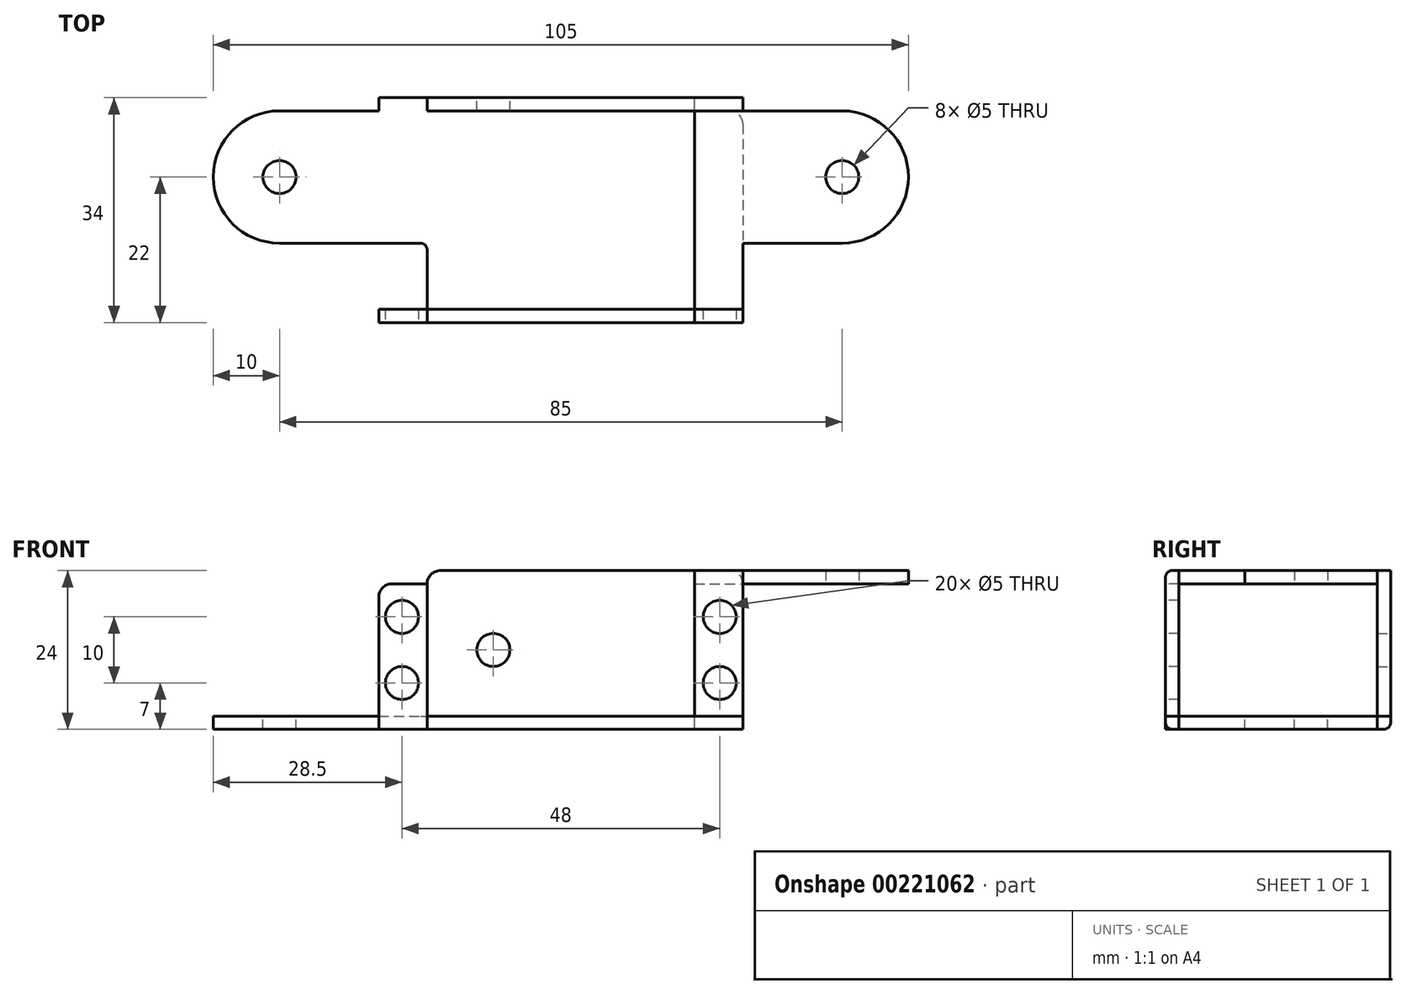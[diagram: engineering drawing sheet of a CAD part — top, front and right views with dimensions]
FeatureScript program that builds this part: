
annotation { "Feature Type Name" : "Feature", "Feature Type Description" : "" }
export const myFeature = defineFeature(function(context is Context, id is Id, definition is map)
    precondition{}
    {
        {
            var Q0;
            Q0=qCreatedBy(makeId("Front.planeOp"),FACE);
            var sketch = newSketch(context, id + "F0", { "sketchPlane" : qUnion([Q0])});
            skLineSegment(sketch, "E0.bottom", {"start": v(-27.5, 10) * mm, "end": v(-20.2, 10) * mm});
            skLineSegment(sketch, "E0.top", {"start": v(-27.5, -10) * mm, "end": v(27.5, -10) * mm});
            skLineSegment(sketch, "E0.left", {"start": v(-27.5, 10) * mm, "end": v(-27.5, -10) * mm});
            skLineSegment(sketch, "E0.right", {"start": v(27.5, 10) * mm, "end": v(27.5, -10) * mm});
            skLineSegment(sketch, "E1", {"start": v(-20.2, 10) * mm, "end": v(-20.2, -10) * mm});
            skLineSegment(sketch, "E2", {"start": v(20.2, 10) * mm, "end": v(20.2, -10) * mm});
            skCircle(sketch, "E3", {"center": v(-24, 5) * mm, "radius": 2.5 * mm});
            skCircle(sketch, "E4", {"center": v(-24, -5) * mm, "radius": 2.5 * mm});
            skCircle(sketch, "E5", {"center": v(24, 5) * mm, "radius": 2.5 * mm});
            skCircle(sketch, "E6", {"center": v(24, -5) * mm, "radius": 2.5 * mm});
            skLineSegment(sketch, "E7", {"start": v(-27.5, -10) * mm, "end": v(-27.5, -12) * mm});
            skLineSegment(sketch, "E8", {"start": v(-27.5, -12) * mm, "end": v(27.5, -12) * mm});
            skLineSegment(sketch, "E9", {"start": v(27.5, -12) * mm, "end": v(27.5, -10) * mm});
            skLineSegment(sketch, "E10", {"start": v(20.2, 10) * mm, "end": v(20.2, 12) * mm});
            skLineSegment(sketch, "E11", {"start": v(20.2, 12) * mm, "end": v(27.5, 12) * mm});
            skLineSegment(sketch, "E12", {"start": v(27.5, 12) * mm, "end": v(27.5, 10) * mm});
            skLineSegment(sketch, "E13.trimOffspring", {"start": v(20.2, 10) * mm, "end": v(27.5, 10) * mm});
            skSolve(sketch);
        }
        {
            var Q0;
            Q0=qCreatedBy(makeId("Top.planeOp"),FACE);
            var sketch = newSketch(context, id + "F1", { "sketchPlane" : qUnion([Q0])});
            skLineSegment(sketch, "E14", {"start": v(-27.5, 34) * mm, "end": v(-27.5, 2) * mm});
            skLineSegment(sketch, "E15", {"start": v(-27.5, 2) * mm, "end": v(20.2, 2) * mm});
            skLineSegment(sketch, "E16", {"start": v(-27.5, 32) * mm, "end": v(42.5, 32) * mm});
            skLineSegment(sketch, "E17", {"start": v(-27.5, 2) * mm, "end": v(-27.5, 0) * mm});
            skLineSegment(sketch, "E18", {"start": v(-27.5, 0) * mm, "end": v(27.5, 0) * mm});
            skCircle(sketch, "E19", {"center": v(42.5, 22) * mm, "radius": 2.5 * mm});
            skLineSegment(sketch, "E20", {"start": v(-27.5, 34) * mm, "end": v(27.5, 34) * mm});
            skLineSegment(sketch, "E21", {"start": v(27.5, 34) * mm, "end": v(27.5, 32) * mm});
            skLineSegment(sketch, "E22", {"start": v(42.5, 12) * mm, "end": v(42.5, 12) * mm});
            skLineSegment(sketch, "E23", {"start": v(42.5, 12) * mm, "end": v(20.2, 12) * mm});
            skLineSegment(sketch, "E24", {"start": v(20.2, 12) * mm, "end": v(20.2, 32) * mm});
            skLineSegment(sketch, "E25", {"start": v(20.2, 12) * mm, "end": v(20.2, 2) * mm});
            skLineSegment(sketch, "E26", {"start": v(20.2, 2) * mm, "end": v(20.2, 0) * mm});
            skLineSegment(sketch, "E27", {"start": v(-20.2, 2) * mm, "end": v(-20.2, 0) * mm});
            skLineSegment(sketch, "E28", {"start": v(-20.2, 32) * mm, "end": v(-20.2, 34) * mm});
            skArc(sketch, "E29", {"start": v(42.5, 12) * mm, "mid": v(52.5, 22) * mm, "end": v(42.5, 32) * mm});
            skLineSegment(sketch, "E30", {"start": v(20.2, 2) * mm, "end": v(27.5, 2) * mm});
            skLineSegment(sketch, "E31", {"start": v(27.5, 2) * mm, "end": v(27.5, 12) * mm});
            skLineSegment(sketch, "E32", {"start": v(27.5, 12) * mm, "end": v(27.5, 2) * mm});
            skLineSegment(sketch, "E33", {"start": v(27.5, 0) * mm, "end": v(27.5, 2) * mm});
            skSolve(sketch);
        }
        {
            var Q0;
            Q0=makeQuery(id+"F0.imprint","IMPRINT",FACE,{"disambiguationData":[TD([[makeQuery(id+"F0.imprint","IMPRINT",EDGE,{"derivedFrom":sQuery(id+"F0.wireOp",EDGE,"E0.bottom")}),-1.0]])]});
            var Q1;
            {var subQ0=sQuery(id+"F0.wireOp",EDGE,"E7");Q1=makeQuery(id+"F0.imprint","IMPRINT",FACE,{"disambiguationData":[TD([[makeQuery(id+"F0.imprint","IMPRINT",EDGE,{"derivedFrom":subQ0}),1.0]])]});}
            var Q2;
            {var subQ0=sQuery(id+"F0.wireOp",EDGE,"E0.right");Q2=makeQuery(id+"F0.imprint","IMPRINT",FACE,{"disambiguationData":[TD([[makeQuery(id+"F0.imprint","IMPRINT",EDGE,{"derivedFrom":subQ0}),-1.0]])]});}
            var Q3;
            Q3=makeQuery(id+"F0.imprint","IMPRINT",FACE,{"disambiguationData":[TD([[makeQuery(id+"F0.imprint","IMPRINT",EDGE,{"derivedFrom":sQuery(id+"F0.wireOp",EDGE,"E10")}),-1.0]])]});
            extrude(context, id + "F2", {"entities" : qUnion([Q0, Q1, Q2, Q3]), "oppositeDirection" : true, "depth" : 2 * mm});
        }
        {
            var Q0;
            {var subQ4=sQuery(id+"F1.wireOp",EDGE,"E15");Q0=makeQuery(id+"F1.imprint","IMPRINT",FACE,{"disambiguationData":[TD([[makeQuery(id+"F1.imprint","IMPRINT",EDGE,{"derivedFrom":subQ4}),1.0]])]});}
            var Q1;
            {var subQ8=sQuery(id+"F1.wireOp",EDGE,"E23");Q1=makeQuery(id+"F1.imprint","IMPRINT",FACE,{"disambiguationData":[TD([[makeQuery(id+"F1.imprint","IMPRINT",EDGE,{"derivedFrom":subQ8}),-1.0]])]});}
            var Q2;
            {var subQ0=sQuery(id+"F1.wireOp",EDGE,"E22");Q2=makeQuery(id+"F1.imprint","IMPRINT",FACE,{"disambiguationData":[TD([[makeQuery(id+"F1.imprint","IMPRINT",EDGE,{"derivedFrom":subQ0}),1.0]])]});}
            var Q3;
            {var subQ0=sQuery(id+"F1.wireOp",EDGE,"E21");Q3=makeQuery(id+"F1.imprint","IMPRINT",FACE,{"disambiguationData":[TD([[makeQuery(id+"F1.imprint","IMPRINT",EDGE,{"derivedFrom":subQ0}),-1.0]])]});}
            var Q4;
            {var subQ0=sQuery(id+"F1.wireOp",EDGE,"E26");Q4=makeQuery(id+"F1.imprint","IMPRINT",FACE,{"disambiguationData":[TD([[makeQuery(id+"F1.imprint","IMPRINT",EDGE,{"derivedFrom":subQ0}),-1.0]])]});}
            var Q5;
            {var subQ0=sQuery(id+"F1.wireOp",EDGE,"E17");Q5=makeQuery(id+"F1.imprint","IMPRINT",FACE,{"disambiguationData":[TD([[makeQuery(id+"F1.imprint","IMPRINT",EDGE,{"derivedFrom":subQ0}),1.0]])]});}
            extrude(context, id + "F3", {"entities" : qUnion([Q0, Q1, Q2, Q3, Q4, Q5]), "oppositeDirection" : true, "depth" : 2 * mm});
        }
        {
            var Q0;
            Q0=makeQuery(id+"F3.opExtrude","SWEPT_BODY",BODY,{"disambiguationData":[OSD([sQuery(id+"F1.wireOp",EDGE,"E14"),sQuery(id+"F1.wireOp",EDGE,"E15"),sQuery(id+"F1.wireOp",EDGE,"q6oPXj39-0zLh-izCR-QsKZ-P5NbTc8Rfou4"),sQuery(id+"F1.wireOp",EDGE,"E16"),sQuery(id+"F1.wireOp",EDGE,"E19"),sQuery(id+"F1.wireOp",EDGE,"E20"),sQuery(id+"F1.wireOp",EDGE,"E21"),sQuery(id+"F1.wireOp",EDGE,"E22")])]});
            var Q1;
            Q1=makeQuery(id+"F2.opExtrude","CAP_EDGE",EDGE,{"disambiguationData":[OSD([sQuery(id+"F0.wireOp",EDGE,"E0.left"),sQuery(id+"F0.wireOp",EDGE,"E7")])],"isStart":false});
            transform(context, id + "F4", {"entities" : qUnion([Q0]), "transformType" : TransformType.TRANSLATION_DISTANCE, "transformDirection" : qUnion([Q1]), "distance" : 10 * mm, "makeCopy" : false});
        }
        {
            var Q0;
            {var subQ8=sQuery(id+"F1.wireOp",EDGE,"E23");Q0=makeQuery(id+"F1.imprint","IMPRINT",FACE,{"disambiguationData":[TD([[makeQuery(id+"F1.imprint","IMPRINT",EDGE,{"derivedFrom":subQ8}),-1.0]])]});}
            var Q1;
            {var subQ0=sQuery(id+"F1.wireOp",EDGE,"E22");Q1=makeQuery(id+"F1.imprint","IMPRINT",FACE,{"disambiguationData":[TD([[makeQuery(id+"F1.imprint","IMPRINT",EDGE,{"derivedFrom":subQ0}),1.0]])]});}
            var Q2;
            {var subQ4=sQuery(id+"F1.wireOp",EDGE,"E23");Q2=makeQuery(id+"F1.imprint","IMPRINT",FACE,{"disambiguationData":[TD([[makeQuery(id+"F1.imprint","IMPRINT",EDGE,{"derivedFrom":subQ4}),1.0]])]});}
            extrude(context, id + "F5", {"entities" : qUnion([Q0, Q1, Q2]), "depth" : 2 * mm});
        }
        {
            var Q0;
            Q0=makeQuery(id+"F5.opExtrude","SWEPT_BODY",BODY,{"disambiguationData":[OSD([sQuery(id+"F1.wireOp",EDGE,"E15"),sQuery(id+"F1.wireOp",EDGE,"q6oPXj39-0zLh-izCR-QsKZ-P5NbTc8Rfou4"),sQuery(id+"F1.wireOp",EDGE,"E16"),sQuery(id+"F1.wireOp",EDGE,"E19"),sQuery(id+"F1.wireOp",EDGE,"E22"),sQuery(id+"F1.wireOp",EDGE,"E24"),sQuery(id+"F1.wireOp",EDGE,"E25")])]});
            var Q1;
            Q1=makeQuery(id+"F2.opExtrude","CAP_EDGE",EDGE,{"disambiguationData":[OSD([sQuery(id+"F0.wireOp",EDGE,"E0.right"),sQuery(id+"F0.wireOp",EDGE,"E9"),sQuery(id+"F0.wireOp",EDGE,"E12")])],"isStart":false});
            transform(context, id + "F6", {"entities" : qUnion([Q0]), "transformType" : TransformType.TRANSLATION_DISTANCE, "transformDirection" : qUnion([Q1]), "distance" : 10 * mm, "makeCopy" : false});
        }
        {
            var Q0;
            Q0=makeQuery(id+"F3.opExtrude","SWEPT_FACE",FACE,{"disambiguationData":[OSD([sQuery(id+"F1.wireOp",EDGE,"E20")])]});
            var sketch = newSketch(context, id + "F7", { "sketchPlane" : qUnion([Q0])});
            skLineSegment(sketch, "E34", {"start": v(-27.5, -11) * mm, "end": v(-27.5, 12) * mm});
            skLineSegment(sketch, "E35", {"start": v(-27.5, 12) * mm, "end": v(20.2, 12) * mm});
            skLineSegment(sketch, "E36", {"start": v(20.2, 12) * mm, "end": v(20.2, -12) * mm});
            skLineSegment(sketch, "E37", {"start": v(20.2, -12) * mm, "end": v(-27.5, -12) * mm});
            skLineSegment(sketch, "E38", {"start": v(-27.5, -12) * mm, "end": v(-27.5, -11) * mm});
            skLineSegment(sketch, "E39", {"start": v(-27.5, -10) * mm, "end": v(20.2, -10) * mm});
            skCircle(sketch, "E40", {"center": v(10.2, 0) * mm, "radius": 2.5 * mm});
            skSolve(sketch);
        }
        {
            var Q0;
            {var subQ2=sQuery(id+"F7.wireOp",EDGE,"E35");Q0=makeQuery(id+"F7.imprint","IMPRINT",FACE,{"disambiguationData":[TD([[makeQuery(id+"F7.imprint","IMPRINT",EDGE,{"derivedFrom":subQ2}),-1.0]])]});}
            extrude(context, id + "F8", {"entities" : qUnion([Q0]), "oppositeDirection" : true, "depth" : 2 * mm});
        }
        {
            var Q0;
            Q0=makeQuery(id+"F3.opExtrude","CAP_EDGE",EDGE,{"disambiguationData":[OSD([sQuery(id+"F1.wireOp",EDGE,"E20")])],"isStart":false});
            fillet(context, id + "F9", {"entities" : qUnion([Q0]), "radius" : 1 * mm, "tangentPropagation" : true, "allowEdgeOverflow" : false});
        }
        {
            var Q0;
            Q0=makeQuery(id+"F2.opExtrude","CAP_EDGE",EDGE,{"disambiguationData":[OSD([sQuery(id+"F0.wireOp",EDGE,"E8")])],"isStart":true});
            fillet(context, id + "F10", {"entities" : qUnion([Q0]), "radius" : 1 * mm, "tangentPropagation" : true, "allowEdgeOverflow" : false});
        }
        {
            var Q0;
            Q0=makeQuery(id+"F2.opExtrude","CAP_EDGE",EDGE,{"disambiguationData":[OSD([sQuery(id+"F0.wireOp",EDGE,"E11")])],"isStart":true});
            fillet(context, id + "F11", {"entities" : qUnion([Q0]), "radius" : 1 * mm, "tangentPropagation" : true, "allowEdgeOverflow" : false});
        }
        {
            var Q0;
            Q0=makeQuery(id+"F8.opExtrude","SWEPT_EDGE",EDGE,{"disambiguationData":[OSD([sQuery(id+"F7.wireOp",EDGE,"E34"),sQuery(id+"F7.wireOp",EDGE,"E35")])]});
            fillet(context, id + "F12", {"entities" : qUnion([Q0]), "radius" : 2 * mm, "tangentPropagation" : true, "allowEdgeOverflow" : false});
        }
        {
            var Q0;
            Q0=makeQuery(id+"F8.opExtrude","SWEPT_EDGE",EDGE,{"disambiguationData":[OSD([sQuery(id+"F7.wireOp",EDGE,"E35"),sQuery(id+"F7.wireOp",EDGE,"E36")])]});
            fillet(context, id + "F13", {"entities" : qUnion([Q0]), "radius" : 2 * mm, "tangentPropagation" : true, "allowEdgeOverflow" : false});
        }
        {
            var Q0;
            Q0=makeQuery(id+"F2.opExtrude","SWEPT_EDGE",EDGE,{"disambiguationData":[OSD([sQuery(id+"F0.wireOp",EDGE,"E0.bottom"),sQuery(id+"F0.wireOp",EDGE,"E0.left")])]});
            fillet(context, id + "F14", {"entities" : qUnion([Q0]), "radius" : 2 * mm, "tangentPropagation" : true, "allowEdgeOverflow" : false});
        }
        {
            var Q0;
            Q0=makeQuery(id+"F3.opExtrude","SWEPT_EDGE",EDGE,{"disambiguationData":[OSD([sQuery(id+"F1.wireOp",EDGE,"E14"),sQuery(id+"F1.wireOp",EDGE,"E16")])]});
            fillet(context, id + "F15", {"entities" : qUnion([Q0]), "radius" : 2 * mm, "tangentPropagation" : true, "allowEdgeOverflow" : false});
        }
        {
            var Q0;
            Q0=makeQuery(id+"F3.opExtrude","SWEPT_EDGE",EDGE,{"disambiguationData":[OSD([sQuery(id+"F1.wireOp",EDGE,"E23"),sQuery(id+"F1.wireOp",EDGE,"E24"),sQuery(id+"F1.wireOp",EDGE,"E25")])]});
            fillet(context, id + "F16", {"entities" : qUnion([Q0]), "radius" : 1 * mm, "tangentPropagation" : true, "allowEdgeOverflow" : false});
        }
        {
            var Q0;
            Q0=makeQuery(id+"F3.opExtrude","SWEPT_BODY",BODY,{"disambiguationData":[OSD([sQuery(id+"F1.wireOp",EDGE,"E14"),sQuery(id+"F1.wireOp",EDGE,"E16"),sQuery(id+"F1.wireOp",EDGE,"E17"),sQuery(id+"F1.wireOp",EDGE,"E18"),sQuery(id+"F1.wireOp",EDGE,"E19"),sQuery(id+"F1.wireOp",EDGE,"E20"),sQuery(id+"F1.wireOp",EDGE,"E21"),sQuery(id+"F1.wireOp",EDGE,"E23"),sQuery(id+"F1.wireOp",EDGE,"E25"),sQuery(id+"F1.wireOp",EDGE,"E26"),sQuery(id+"F1.wireOp",EDGE,"E28"),sQuery(id+"F1.wireOp",EDGE,"E29")])]});
            var Q1;
            Q1=qCreatedBy(makeId("Right.planeOp"),FACE);
            mirror(context, id + "F17", {"entities" : qUnion([Q0]), "mirrorPlane" : qUnion([Q1])});
        }
        {
            var Q0;
            Q0=makeQuery(id+"F3.opExtrude","SWEPT_BODY",BODY,{"disambiguationData":[OSD([sQuery(id+"F1.wireOp",EDGE,"E14"),sQuery(id+"F1.wireOp",EDGE,"E16"),sQuery(id+"F1.wireOp",EDGE,"E17"),sQuery(id+"F1.wireOp",EDGE,"E18"),sQuery(id+"F1.wireOp",EDGE,"E19"),sQuery(id+"F1.wireOp",EDGE,"E20"),sQuery(id+"F1.wireOp",EDGE,"E21"),sQuery(id+"F1.wireOp",EDGE,"E23"),sQuery(id+"F1.wireOp",EDGE,"E25"),sQuery(id+"F1.wireOp",EDGE,"E26"),sQuery(id+"F1.wireOp",EDGE,"E28"),sQuery(id+"F1.wireOp",EDGE,"E29")])]});
            deleteBodies(context, id + "F18", {"entities" : qUnion([Q0])});
        }
    });
